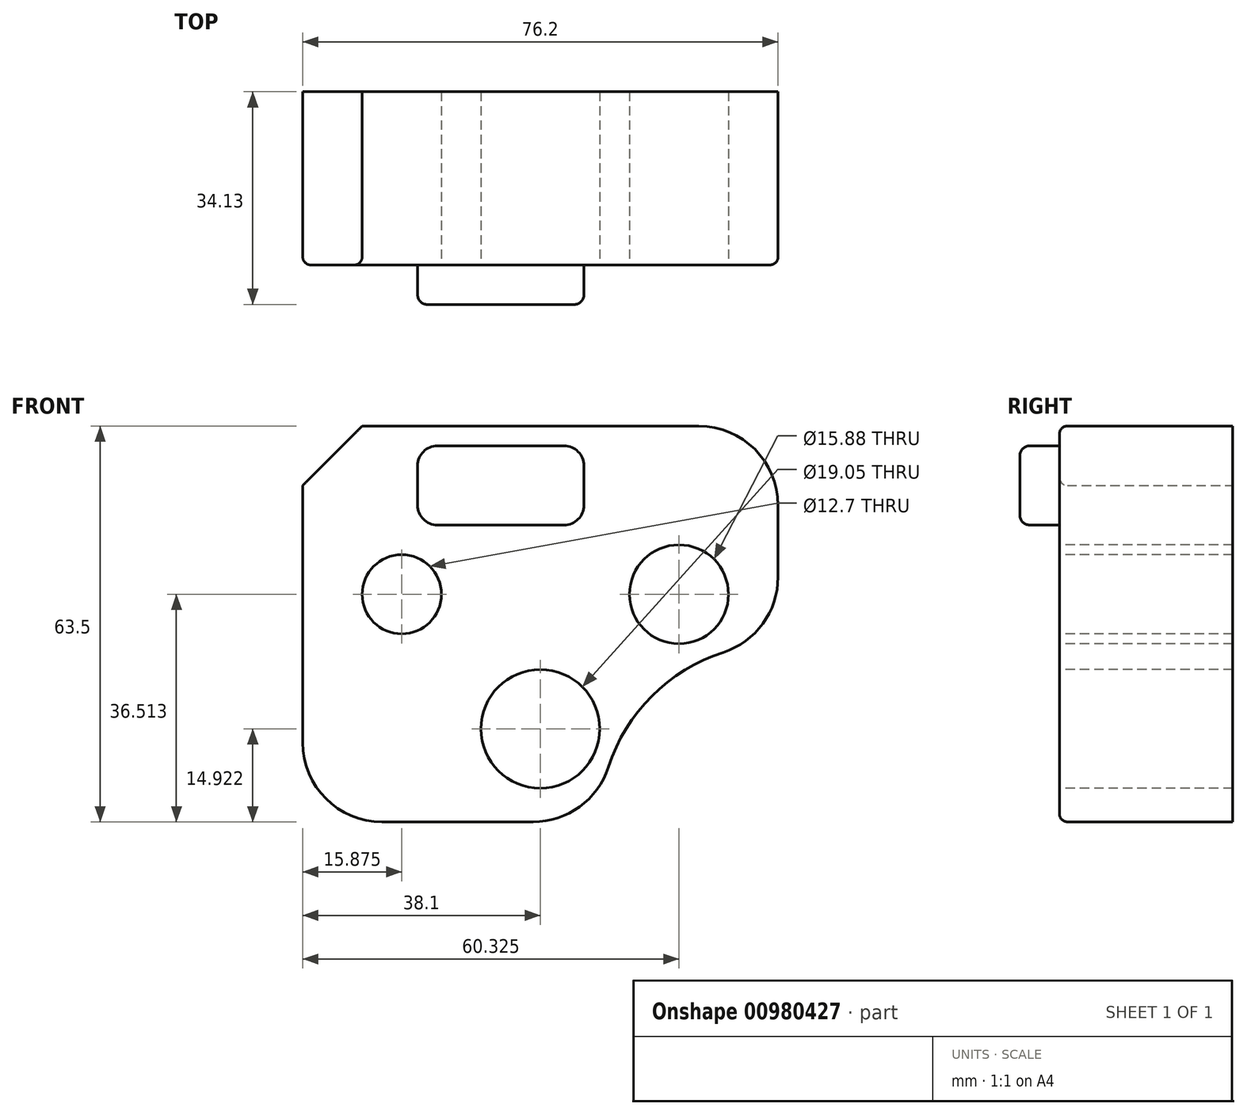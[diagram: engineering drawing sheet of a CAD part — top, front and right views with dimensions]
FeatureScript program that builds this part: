
annotation { "Feature Type Name" : "Feature", "Feature Type Description" : "" }
export const myFeature = defineFeature(function(context is Context, id is Id, definition is map)
    precondition{}
    {
        {
            var Q0;
            Q0=qCreatedBy(makeId("Front.planeOp"),FACE);
            var sketch = newSketch(context, id + "F0", { "sketchPlane" : qUnion([Q0])});
            skLineSegment(sketch, "E0.bottom", {"start": v(38.1, 31.75) * mm, "end": v(-38.1, 31.75) * mm});
            skLineSegment(sketch, "E0.top", {"start": v(38.1, -31.75) * mm, "end": v(-38.1, -31.75) * mm});
            skLineSegment(sketch, "E0.left", {"start": v(38.1, 31.75) * mm, "end": v(38.1, -31.75) * mm});
            skLineSegment(sketch, "E0.right", {"start": v(-38.1, 31.75) * mm, "end": v(-38.1, -31.75) * mm});
            skPoint(sketch, "E0.middle", {"position": v(0, 0) * mm});
            skSolve(sketch);
        }
        {
            var Q0;
            Q0 = qSketchRegion(id + "F0", true);
            extrude(context, id + "F1", {"entities" : qUnion([Q0]), "depth" : 27.78 * mm, "offsetDistance" : 25.4 * mm});
        }
        {
            var Q0;
            Q0=makeQuery(id+"F1.opExtrude","CAP_FACE",FACE,{"disambiguationData":[OSD([sQuery(id+"F0.wireOp",EDGE,"E0.bottom"),sQuery(id+"F0.wireOp",EDGE,"E0.top"),sQuery(id+"F0.wireOp",EDGE,"E0.left"),sQuery(id+"F0.wireOp",EDGE,"E0.right")])],"isStart":false});
            var sketch = newSketch(context, id + "F2", { "sketchPlane" : qUnion([Q0])});
            skCircle(sketch, "E1", {"center": v(-22.22, 4.76) * mm, "radius": 6.35 * mm});
            skCircle(sketch, "E2", {"center": v(0, -16.83) * mm, "radius": 9.53 * mm});
            skCircle(sketch, "E3", {"center": v(22.22, 4.76) * mm, "radius": 7.94 * mm});
            skLineSegment(sketch, "E4", {"start": v(-22.22, 4.76) * mm, "end": v(22.22, 4.76) * mm, "construction": true});
            skPoint(sketch, "E5", {"position": v(0, 4.76) * mm});
            skSolve(sketch);
        }
        {
            var Q0;
            Q0 = qSketchRegion(id + "F2", true);
            extrude(context, id + "F3", {"entities" : qUnion([Q0]), "operationType" : NewBodyOperationType.REMOVE, "endBound" : BoundingType.THROUGH_ALL, "oppositeDirection" : true, "depth" : 68.7 * mm, "offsetDistance" : 25.4 * mm});
        }
        {
            var Q0;
            Q0=makeQuery(id+"F1.opExtrude","SWEPT_EDGE",EDGE,{"disambiguationData":[OSD([sQuery(id+"F0.wireOp",EDGE,"E0.bottom"),sQuery(id+"F0.wireOp",EDGE,"E0.left")])]});
            fillet(context, id + "F4", {"entities" : qUnion([Q0]), "radius" : 12.7 * mm, "tangentPropagation" : true, "allowEdgeOverflow" : false});
        }
        {
            var Q0;
            Q0=makeQuery(id+"F1.opExtrude","SWEPT_EDGE",EDGE,{"disambiguationData":[OSD([sQuery(id+"F0.wireOp",EDGE,"E0.bottom"),sQuery(id+"F0.wireOp",EDGE,"E0.right")])]});
            chamfer(context, id + "F5", {"entities" : qUnion([Q0]), "width" : 9.52 * mm, "tangentPropagation" : true});
        }
        {
            var Q0;
            Q0=makeQuery(id+"F1.opExtrude","CAP_FACE",FACE,{"disambiguationData":[OSD([sQuery(id+"F0.wireOp",EDGE,"E0.bottom"),sQuery(id+"F0.wireOp",EDGE,"E0.top"),sQuery(id+"F0.wireOp",EDGE,"E0.left"),sQuery(id+"F0.wireOp",EDGE,"E0.right")])],"isStart":false});
            var sketch = newSketch(context, id + "F6", { "sketchPlane" : qUnion([Q0])});
            skCircle(sketch, "E6", {"center": v(38.1, -31.75) * mm, "radius": 28.58 * mm});
            skSolve(sketch);
        }
        {
            var Q0;
            Q0 = qSketchRegion(id + "F6", true);
            extrude(context, id + "F7", {"entities" : qUnion([Q0]), "operationType" : NewBodyOperationType.REMOVE, "endBound" : BoundingType.THROUGH_ALL, "oppositeDirection" : true, "depth" : 25.4 * mm, "offsetDistance" : 25.4 * mm});
        }
        {
            var Q0;
            Q0=makeQuery(id+"F1.opExtrude","SWEPT_EDGE",EDGE,{"disambiguationData":[OSD([sQuery(id+"F0.wireOp",EDGE,"E0.top"),sQuery(id+"F0.wireOp",EDGE,"E0.right")])]});
            var Q1;
            Q1=makeQuery(id+"F7.boolean.opBoolean","INTERSECT",EDGE,{"derivedFrom":[makeQuery(id+"F1.opExtrude","SWEPT_FACE",FACE,{"disambiguationData":[OSD([sQuery(id+"F0.wireOp",EDGE,"E0.top")])]}),makeQuery(id+"F7.opExtrude","SWEPT_FACE",FACE,{"disambiguationData":[OSD([sQuery(id+"F6.wireOp",EDGE,"E6")])]})]});
            var Q2;
            Q2=makeQuery(id+"F7.boolean.opBoolean","INTERSECT",EDGE,{"derivedFrom":[makeQuery(id+"F1.opExtrude","SWEPT_FACE",FACE,{"disambiguationData":[OSD([sQuery(id+"F0.wireOp",EDGE,"E0.left")])]}),makeQuery(id+"F7.opExtrude","SWEPT_FACE",FACE,{"disambiguationData":[OSD([sQuery(id+"F6.wireOp",EDGE,"E6")])]})]});
            fillet(context, id + "F8", {"entities" : qUnion([Q0, Q1, Q2]), "radius" : 12.7 * mm, "tangentPropagation" : true, "allowEdgeOverflow" : false});
        }
        {
            var Q0;
            Q0=makeQuery(id+"F1.opExtrude","CAP_FACE",FACE,{"disambiguationData":[OSD([sQuery(id+"F0.wireOp",EDGE,"E0.bottom"),sQuery(id+"F0.wireOp",EDGE,"E0.top"),sQuery(id+"F0.wireOp",EDGE,"E0.left"),sQuery(id+"F0.wireOp",EDGE,"E0.right")])],"isStart":false});
            var sketch = newSketch(context, id + "F9", { "sketchPlane" : qUnion([Q0])});
            skLineSegment(sketch, "E7.bottom", {"start": v(-16.5, 15.88) * mm, "end": v(3.81, 15.88) * mm});
            skLineSegment(sketch, "E7.top", {"start": v(-16.5, 28.58) * mm, "end": v(3.81, 28.58) * mm});
            skLineSegment(sketch, "E7.left", {"start": v(-19.68, 19.05) * mm, "end": v(-19.68, 25.4) * mm});
            skLineSegment(sketch, "E7.right", {"start": v(6.99, 19.05) * mm, "end": v(6.99, 25.4) * mm});
            skPoint(sketch, "E7.middle", {"position": v(-6.35, 22.23) * mm});
            skLineSegment(sketch, "E8.left", {"start": v(-9.9, 23.14) * mm, "end": v(-9.9, 23.14) * mm});
            skLineSegment(sketch, "E8.right", {"start": v(-19.34, 23.14) * mm, "end": v(-19.34, 23.14) * mm});
            skPoint(sketch, "E9.visualSharp", {"position": v(6.99, 28.58) * mm});
            skArc(sketch, "E9.filletArc", {"start": v(6.99, 25.4) * mm, "mid": v(6.06, 27.65) * mm, "end": v(3.81, 28.58) * mm});
            skPoint(sketch, "E10.visualSharp", {"position": v(6.99, 15.88) * mm});
            skArc(sketch, "E10.filletArc", {"start": v(3.81, 15.88) * mm, "mid": v(6.06, 16.8) * mm, "end": v(6.99, 19.05) * mm});
            skPoint(sketch, "E11.visualSharp", {"position": v(-19.68, 15.88) * mm});
            skArc(sketch, "E11.filletArc", {"start": v(-19.68, 19.05) * mm, "mid": v(-18.76, 16.8) * mm, "end": v(-16.5, 15.88) * mm});
            skPoint(sketch, "E12.visualSharp", {"position": v(-19.68, 28.58) * mm});
            skArc(sketch, "E12.filletArc", {"start": v(-16.5, 28.58) * mm, "mid": v(-18.76, 27.65) * mm, "end": v(-19.68, 25.4) * mm});
            skSolve(sketch);
        }
        {
            var Q0;
            Q0 = qSketchRegion(id + "F9", true);
            extrude(context, id + "F10", {"entities" : qUnion([Q0]), "operationType" : NewBodyOperationType.ADD, "depth" : 6.35 * mm, "offsetDistance" : 25.4 * mm});
        }
        {
            var Q0;
            Q0=makeQuery(id+"F10.opExtrude","CAP_FACE",FACE,{"disambiguationData":[OSD([sQuery(id+"F9.wireOp",EDGE,"E7.bottom"),sQuery(id+"F9.wireOp",EDGE,"E7.top"),sQuery(id+"F9.wireOp",EDGE,"E7.left"),sQuery(id+"F9.wireOp",EDGE,"E7.right"),sQuery(id+"F9.wireOp",EDGE,"E9.filletArc"),sQuery(id+"F9.wireOp",EDGE,"E10.filletArc"),sQuery(id+"F9.wireOp",EDGE,"E11.filletArc"),sQuery(id+"F9.wireOp",EDGE,"E12.filletArc")])],"isStart":false});
            var Q1;
            Q1=makeQuery(id+"F10.opExtrude","CAP_EDGE",EDGE,{"disambiguationData":[OSD([sQuery(id+"F9.wireOp",EDGE,"E7.top")])],"isStart":true});
            fillet(context, id + "F11", {"entities" : qUnion([Q0, Q1]), "radius" : 1.57 * mm, "tangentPropagation" : true, "allowEdgeOverflow" : false});
        }
        {
            var Q0;
            Q0=makeQuery(id+"F3.boolean.opBoolean","COPY",EDGE,{"derivedFrom":makeQuery(id+"F3.opExtrude","CAP_EDGE",EDGE,{"disambiguationData":[OSD([sQuery(id+"F2.wireOp",EDGE,"E1")])],"isStart":true})});
            var Q1;
            Q1=makeQuery(id+"F3.boolean.opBoolean","COPY",EDGE,{"derivedFrom":makeQuery(id+"F3.opExtrude","CAP_EDGE",EDGE,{"disambiguationData":[OSD([sQuery(id+"F2.wireOp",EDGE,"E2")])],"isStart":true})});
            var Q2;
            Q2=makeQuery(id+"F3.boolean.opBoolean","COPY",EDGE,{"derivedFrom":makeQuery(id+"F3.opExtrude","CAP_EDGE",EDGE,{"disambiguationData":[OSD([sQuery(id+"F2.wireOp",EDGE,"E3")])],"isStart":true})});
            var Q3;
            Q3=makeQuery(id+"F1.opExtrude","CAP_EDGE",EDGE,{"disambiguationData":[OSD([sQuery(id+"F0.wireOp",EDGE,"E0.top")])],"isStart":false});
            fillet(context, id + "F12", {"entities" : qUnion([Q0, Q1, Q2, Q3]), "radius" : 1.27 * mm, "tangentPropagation" : true, "allowEdgeOverflow" : false});
        }
    });
